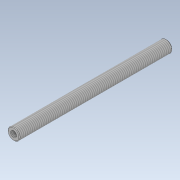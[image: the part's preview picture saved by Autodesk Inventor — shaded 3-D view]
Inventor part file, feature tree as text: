
AUTODESK INVENTOR PART (.ipt)
format: ipt  version: 2021 (Build 250183000, 183)  size: 92,672 bytes
history: native  units: mm
features: other x1, revolve x1, thread x1, chamfer x1, sketch x1
ambient origin geometry x8: Origin, YZ Plane, XZ Plane, XY Plane, X Axis, Y Axis, Z Axis, Center Point
bodies: Body1 (feature_tree)
feature tree (5):
  other  "Sólido1"
  revolve  "Revolución1"  [1 undecoded]
  thread  "Rosca1"  [1 undecoded]
  chamfer  "Chaflán1"  Angle=90.0deg  [1 undecoded]
  sketch  "Boceto1"  dims[d0=130.0mm d1=10.0mm d2=3.0mm d3=90.0deg d4=130.0mm d5=0.0mm d6=0.5mm d7=2.0mm d8=45.0deg]
note: 3 required parameter values undecoded (feature->parameter linkage not recoverable at this tier; creation-order binding heuristic only, values carry confidence <= 0.55)